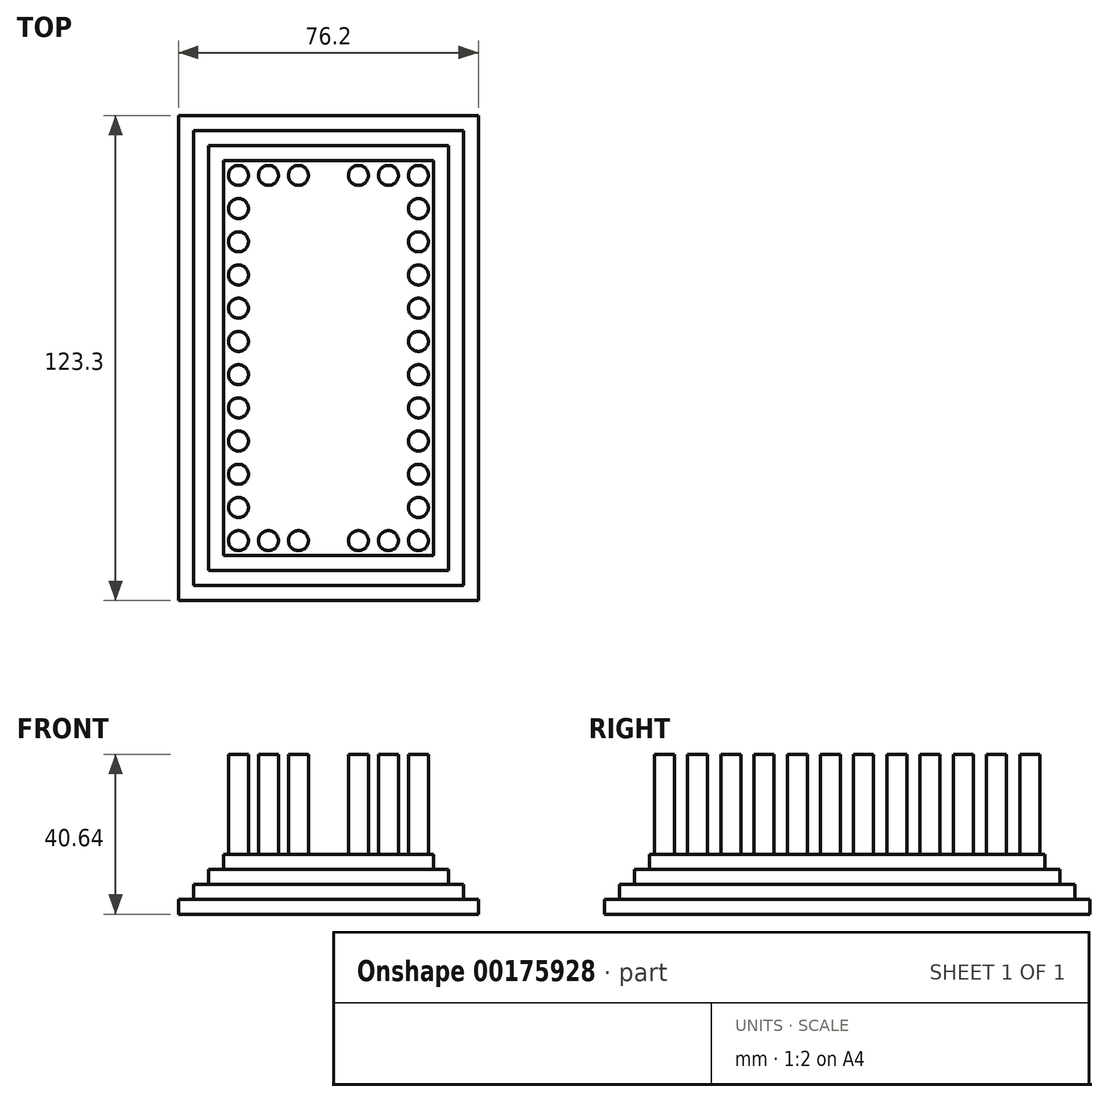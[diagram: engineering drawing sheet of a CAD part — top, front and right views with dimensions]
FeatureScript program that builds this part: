
annotation { "Feature Type Name" : "Feature", "Feature Type Description" : "" }
export const myFeature = defineFeature(function(context is Context, id is Id, definition is map)
    precondition{}
    {
        {
            var Q0;
            Q0=qCreatedBy(makeId("Top.planeOp"),FACE);
            var sketch = newSketch(context, id + "F0", { "sketchPlane" : qUnion([Q0])});
            skLineSegment(sketch, "E0.bottom", {"start": v(38.1, 61.65) * mm, "end": v(-38.1, 61.65) * mm});
            skLineSegment(sketch, "E0.top", {"start": v(38.1, -61.65) * mm, "end": v(-38.1, -61.65) * mm});
            skLineSegment(sketch, "E0.left", {"start": v(38.1, 61.65) * mm, "end": v(38.1, -61.65) * mm});
            skLineSegment(sketch, "E0.right", {"start": v(-38.1, 61.65) * mm, "end": v(-38.1, -61.65) * mm});
            skPoint(sketch, "E0.middle", {"position": v(0, 0) * mm});
            skLineSegment(sketch, "E1.bottom", {"start": v(-34.3, 57.84) * mm, "end": v(34.3, 57.84) * mm});
            skLineSegment(sketch, "E1.top", {"start": v(-34.3, -57.84) * mm, "end": v(34.3, -57.84) * mm});
            skLineSegment(sketch, "E1.left", {"start": v(-34.3, 57.84) * mm, "end": v(-34.3, -57.84) * mm});
            skLineSegment(sketch, "E1.right", {"start": v(34.3, 57.84) * mm, "end": v(34.3, -57.84) * mm});
            skLineSegment(sketch, "E2.bottom", {"start": v(-30.48, 54.03) * mm, "end": v(30.48, 54.03) * mm});
            skLineSegment(sketch, "E2.top", {"start": v(-30.48, -54.03) * mm, "end": v(30.48, -54.03) * mm});
            skLineSegment(sketch, "E2.left", {"start": v(-30.48, 54.03) * mm, "end": v(-30.48, -54.03) * mm});
            skLineSegment(sketch, "E2.right", {"start": v(30.48, 54.03) * mm, "end": v(30.48, -54.03) * mm});
            skLineSegment(sketch, "E3.bottom", {"start": v(26.67, 50.22) * mm, "end": v(-26.67, 50.22) * mm});
            skLineSegment(sketch, "E3.top", {"start": v(26.67, -50.22) * mm, "end": v(-26.67, -50.22) * mm});
            skLineSegment(sketch, "E3.left", {"start": v(26.67, 50.22) * mm, "end": v(26.67, -50.22) * mm});
            skLineSegment(sketch, "E3.right", {"start": v(-26.67, 50.22) * mm, "end": v(-26.67, -50.22) * mm});
            skSolve(sketch);
        }
        {
            var Q0;
            Q0=makeQuery(id+"F0.imprint","IMPRINT",FACE,{"disambiguationData":[TD([[makeQuery(id+"F0.imprint","IMPRINT",EDGE,{"derivedFrom":sQuery(id+"F0.wireOp",EDGE,"E0.bottom")}),1.0]])]});
            extrude(context, id + "F1", {"entities" : qUnion([Q0]), "depth" : 3.8 * mm});
        }
        {
            var Q0;
            Q0=makeQuery(id+"F0.imprint","IMPRINT",FACE,{"disambiguationData":[TD([[makeQuery(id+"F0.imprint","IMPRINT",EDGE,{"derivedFrom":sQuery(id+"F0.wireOp",EDGE,"E1.bottom")}),-1.0]])]});
            extrude(context, id + "F2", {"entities" : qUnion([Q0]), "operationType" : NewBodyOperationType.ADD, "depth" : 7.62 * mm});
        }
        {
            var Q0;
            Q0=makeQuery(id+"F0.imprint","IMPRINT",FACE,{"disambiguationData":[TD([[makeQuery(id+"F0.imprint","IMPRINT",EDGE,{"derivedFrom":sQuery(id+"F0.wireOp",EDGE,"E2.bottom")}),-1.0]])]});
            extrude(context, id + "F3", {"entities" : qUnion([Q0]), "operationType" : NewBodyOperationType.ADD, "depth" : 11.43 * mm});
        }
        {
            var Q0;
            Q0=makeQuery(id+"F0.imprint","IMPRINT",FACE,{"disambiguationData":[TD([[makeQuery(id+"F0.imprint","IMPRINT",EDGE,{"derivedFrom":sQuery(id+"F0.wireOp",EDGE,"E3.bottom")}),1.0]])]});
            extrude(context, id + "F4", {"entities" : qUnion([Q0]), "operationType" : NewBodyOperationType.ADD, "depth" : 15.24 * mm});
        }
        {
            var Q0;
            Q0=makeQuery(id+"F4.opExtrude","CAP_FACE",FACE,{"disambiguationData":[OSD([sQuery(id+"F0.wireOp",EDGE,"E3.bottom"),sQuery(id+"F0.wireOp",EDGE,"E3.top"),sQuery(id+"F0.wireOp",EDGE,"E3.left"),sQuery(id+"F0.wireOp",EDGE,"E3.right")])],"isStart":false});
            var sketch = newSketch(context, id + "F5", { "sketchPlane" : qUnion([Q0])});
            skPoint(sketch, "E4.middle", {"position": v(0, 0) * mm});
            skCircle(sketch, "E5", {"center": v(-22.86, 46.4) * mm, "radius": 2.54 * mm});
            skCircle(sketch, "E6", {"center": v(22.86, 46.4) * mm, "radius": 2.54 * mm});
            skCircle(sketch, "E7", {"center": v(-22.86, -46.4) * mm, "radius": 2.54 * mm});
            skCircle(sketch, "E8", {"center": v(22.86, -46.4) * mm, "radius": 2.54 * mm});
            skPoint(sketch, "E9", {"position": v(0, 46.4) * mm});
            skCircle(sketch, "E10", {"center": v(-15.24, 46.4) * mm, "radius": 2.54 * mm});
            skCircle(sketch, "E11", {"center": v(-7.62, 46.4) * mm, "radius": 2.54 * mm});
            skCircle(sketch, "E12", {"center": v(7.62, 46.4) * mm, "radius": 2.54 * mm});
            skCircle(sketch, "E13", {"center": v(15.24, 46.4) * mm, "radius": 2.54 * mm});
            skCircle(sketch, "E14", {"center": v(-15.24, -46.4) * mm, "radius": 2.54 * mm});
            skCircle(sketch, "E15", {"center": v(-7.62, -46.4) * mm, "radius": 2.54 * mm});
            skCircle(sketch, "E16", {"center": v(7.62, -46.4) * mm, "radius": 2.54 * mm});
            skCircle(sketch, "E17", {"center": v(15.24, -46.4) * mm, "radius": 2.54 * mm});
            skCircle(sketch, "E18", {"center": v(-22.86, -37.97) * mm, "radius": 2.54 * mm});
            skCircle(sketch, "E19", {"center": v(-22.86, -29.53) * mm, "radius": 2.54 * mm});
            skCircle(sketch, "E20", {"center": v(-22.86, -21.1) * mm, "radius": 2.54 * mm});
            skCircle(sketch, "E21", {"center": v(-22.86, -12.66) * mm, "radius": 2.54 * mm});
            skCircle(sketch, "E22", {"center": v(-22.86, -4.22) * mm, "radius": 2.54 * mm});
            skCircle(sketch, "E23", {"center": v(-22.86, 4.22) * mm, "radius": 2.54 * mm});
            skCircle(sketch, "E24", {"center": v(-22.86, 12.66) * mm, "radius": 2.54 * mm});
            skCircle(sketch, "E25", {"center": v(-22.86, 21.1) * mm, "radius": 2.54 * mm});
            skCircle(sketch, "E26", {"center": v(-22.86, 29.53) * mm, "radius": 2.54 * mm});
            skCircle(sketch, "E27", {"center": v(-22.86, 37.96) * mm, "radius": 2.54 * mm});
            skCircle(sketch, "E28", {"center": v(22.86, -37.97) * mm, "radius": 2.54 * mm});
            skCircle(sketch, "E29", {"center": v(22.86, -29.53) * mm, "radius": 2.54 * mm});
            skCircle(sketch, "E30", {"center": v(22.86, -21.1) * mm, "radius": 2.54 * mm});
            skCircle(sketch, "E31", {"center": v(22.86, -12.66) * mm, "radius": 2.54 * mm});
            skCircle(sketch, "E32", {"center": v(22.86, -4.22) * mm, "radius": 2.54 * mm});
            skCircle(sketch, "E33", {"center": v(22.86, 4.22) * mm, "radius": 2.54 * mm});
            skCircle(sketch, "E34", {"center": v(22.86, 12.66) * mm, "radius": 2.54 * mm});
            skCircle(sketch, "E35", {"center": v(22.86, 21.1) * mm, "radius": 2.54 * mm});
            skCircle(sketch, "E36", {"center": v(22.86, 29.53) * mm, "radius": 2.54 * mm});
            skCircle(sketch, "E37", {"center": v(22.86, 37.97) * mm, "radius": 2.54 * mm});
            skSolve(sketch);
        }
        {
            var Q0;
            Q0=makeQuery(id+"F5.imprint","IMPRINT",FACE,{"disambiguationData":[TD([[makeQuery(id+"F5.imprint","IMPRINT",EDGE,{"derivedFrom":sQuery(id+"F5.wireOp",EDGE,"E10")}),1.0]])]});
            var Q1;
            Q1=makeQuery(id+"F5.imprint","IMPRINT",FACE,{"disambiguationData":[TD([[makeQuery(id+"F5.imprint","IMPRINT",EDGE,{"derivedFrom":sQuery(id+"F5.wireOp",EDGE,"E5")}),1.0]])]});
            var Q2;
            Q2=makeQuery(id+"F5.imprint","IMPRINT",FACE,{"disambiguationData":[TD([[makeQuery(id+"F5.imprint","IMPRINT",EDGE,{"derivedFrom":sQuery(id+"F5.wireOp",EDGE,"E11")}),1.0]])]});
            var Q3;
            Q3=makeQuery(id+"F5.imprint","IMPRINT",FACE,{"disambiguationData":[TD([[makeQuery(id+"F5.imprint","IMPRINT",EDGE,{"derivedFrom":sQuery(id+"F5.wireOp",EDGE,"E27")}),1.0]])]});
            var Q4;
            Q4=makeQuery(id+"F5.imprint","IMPRINT",FACE,{"disambiguationData":[TD([[makeQuery(id+"F5.imprint","IMPRINT",EDGE,{"derivedFrom":sQuery(id+"F5.wireOp",EDGE,"E26")}),1.0]])]});
            var Q5;
            Q5=makeQuery(id+"F5.imprint","IMPRINT",FACE,{"disambiguationData":[TD([[makeQuery(id+"F5.imprint","IMPRINT",EDGE,{"derivedFrom":sQuery(id+"F5.wireOp",EDGE,"E25")}),1.0]])]});
            var Q6;
            Q6=makeQuery(id+"F5.imprint","IMPRINT",FACE,{"disambiguationData":[TD([[makeQuery(id+"F5.imprint","IMPRINT",EDGE,{"derivedFrom":sQuery(id+"F5.wireOp",EDGE,"E24")}),1.0]])]});
            var Q7;
            Q7=makeQuery(id+"F5.imprint","IMPRINT",FACE,{"disambiguationData":[TD([[makeQuery(id+"F5.imprint","IMPRINT",EDGE,{"derivedFrom":sQuery(id+"F5.wireOp",EDGE,"E23")}),1.0]])]});
            var Q8;
            Q8=makeQuery(id+"F5.imprint","IMPRINT",FACE,{"disambiguationData":[TD([[makeQuery(id+"F5.imprint","IMPRINT",EDGE,{"derivedFrom":sQuery(id+"F5.wireOp",EDGE,"E22")}),1.0]])]});
            var Q9;
            Q9=makeQuery(id+"F5.imprint","IMPRINT",FACE,{"disambiguationData":[TD([[makeQuery(id+"F5.imprint","IMPRINT",EDGE,{"derivedFrom":sQuery(id+"F5.wireOp",EDGE,"E21")}),1.0]])]});
            var Q10;
            Q10=makeQuery(id+"F5.imprint","IMPRINT",FACE,{"disambiguationData":[TD([[makeQuery(id+"F5.imprint","IMPRINT",EDGE,{"derivedFrom":sQuery(id+"F5.wireOp",EDGE,"E12")}),1.0]])]});
            var Q11;
            Q11=makeQuery(id+"F5.imprint","IMPRINT",FACE,{"disambiguationData":[TD([[makeQuery(id+"F5.imprint","IMPRINT",EDGE,{"derivedFrom":sQuery(id+"F5.wireOp",EDGE,"E13")}),1.0]])]});
            var Q12;
            Q12=makeQuery(id+"F5.imprint","IMPRINT",FACE,{"disambiguationData":[TD([[makeQuery(id+"F5.imprint","IMPRINT",EDGE,{"derivedFrom":sQuery(id+"F5.wireOp",EDGE,"E6")}),1.0]])]});
            var Q13;
            Q13=makeQuery(id+"F5.imprint","IMPRINT",FACE,{"disambiguationData":[TD([[makeQuery(id+"F5.imprint","IMPRINT",EDGE,{"derivedFrom":sQuery(id+"F5.wireOp",EDGE,"E37")}),1.0]])]});
            var Q14;
            Q14=makeQuery(id+"F5.imprint","IMPRINT",FACE,{"disambiguationData":[TD([[makeQuery(id+"F5.imprint","IMPRINT",EDGE,{"derivedFrom":sQuery(id+"F5.wireOp",EDGE,"E36")}),1.0]])]});
            var Q15;
            Q15=makeQuery(id+"F5.imprint","IMPRINT",FACE,{"disambiguationData":[TD([[makeQuery(id+"F5.imprint","IMPRINT",EDGE,{"derivedFrom":sQuery(id+"F5.wireOp",EDGE,"E35")}),1.0]])]});
            var Q16;
            Q16=makeQuery(id+"F5.imprint","IMPRINT",FACE,{"disambiguationData":[TD([[makeQuery(id+"F5.imprint","IMPRINT",EDGE,{"derivedFrom":sQuery(id+"F5.wireOp",EDGE,"E34")}),1.0]])]});
            var Q17;
            Q17=makeQuery(id+"F5.imprint","IMPRINT",FACE,{"disambiguationData":[TD([[makeQuery(id+"F5.imprint","IMPRINT",EDGE,{"derivedFrom":sQuery(id+"F5.wireOp",EDGE,"E33")}),1.0]])]});
            var Q18;
            Q18=makeQuery(id+"F5.imprint","IMPRINT",FACE,{"disambiguationData":[TD([[makeQuery(id+"F5.imprint","IMPRINT",EDGE,{"derivedFrom":sQuery(id+"F5.wireOp",EDGE,"E32")}),1.0]])]});
            var Q19;
            Q19=makeQuery(id+"F5.imprint","IMPRINT",FACE,{"disambiguationData":[TD([[makeQuery(id+"F5.imprint","IMPRINT",EDGE,{"derivedFrom":sQuery(id+"F5.wireOp",EDGE,"E31")}),1.0]])]});
            var Q20;
            Q20=makeQuery(id+"F5.imprint","IMPRINT",FACE,{"disambiguationData":[TD([[makeQuery(id+"F5.imprint","IMPRINT",EDGE,{"derivedFrom":sQuery(id+"F5.wireOp",EDGE,"E20")}),1.0]])]});
            var Q21;
            Q21=makeQuery(id+"F5.imprint","IMPRINT",FACE,{"disambiguationData":[TD([[makeQuery(id+"F5.imprint","IMPRINT",EDGE,{"derivedFrom":sQuery(id+"F5.wireOp",EDGE,"E19")}),1.0]])]});
            var Q22;
            Q22=makeQuery(id+"F5.imprint","IMPRINT",FACE,{"disambiguationData":[TD([[makeQuery(id+"F5.imprint","IMPRINT",EDGE,{"derivedFrom":sQuery(id+"F5.wireOp",EDGE,"E18")}),1.0]])]});
            var Q23;
            Q23=makeQuery(id+"F5.imprint","IMPRINT",FACE,{"disambiguationData":[TD([[makeQuery(id+"F5.imprint","IMPRINT",EDGE,{"derivedFrom":sQuery(id+"F5.wireOp",EDGE,"E7")}),1.0]])]});
            var Q24;
            Q24=makeQuery(id+"F5.imprint","IMPRINT",FACE,{"disambiguationData":[TD([[makeQuery(id+"F5.imprint","IMPRINT",EDGE,{"derivedFrom":sQuery(id+"F5.wireOp",EDGE,"E14")}),1.0]])]});
            var Q25;
            Q25=makeQuery(id+"F5.imprint","IMPRINT",FACE,{"disambiguationData":[TD([[makeQuery(id+"F5.imprint","IMPRINT",EDGE,{"derivedFrom":sQuery(id+"F5.wireOp",EDGE,"E15")}),1.0]])]});
            var Q26;
            Q26=makeQuery(id+"F5.imprint","IMPRINT",FACE,{"disambiguationData":[TD([[makeQuery(id+"F5.imprint","IMPRINT",EDGE,{"derivedFrom":sQuery(id+"F5.wireOp",EDGE,"E16")}),1.0]])]});
            var Q27;
            Q27=makeQuery(id+"F5.imprint","IMPRINT",FACE,{"disambiguationData":[TD([[makeQuery(id+"F5.imprint","IMPRINT",EDGE,{"derivedFrom":sQuery(id+"F5.wireOp",EDGE,"E17")}),1.0]])]});
            var Q28;
            Q28=makeQuery(id+"F5.imprint","IMPRINT",FACE,{"disambiguationData":[TD([[makeQuery(id+"F5.imprint","IMPRINT",EDGE,{"derivedFrom":sQuery(id+"F5.wireOp",EDGE,"E8")}),1.0]])]});
            var Q29;
            Q29=makeQuery(id+"F5.imprint","IMPRINT",FACE,{"disambiguationData":[TD([[makeQuery(id+"F5.imprint","IMPRINT",EDGE,{"derivedFrom":sQuery(id+"F5.wireOp",EDGE,"E28")}),1.0]])]});
            var Q30;
            Q30=makeQuery(id+"F5.imprint","IMPRINT",FACE,{"disambiguationData":[TD([[makeQuery(id+"F5.imprint","IMPRINT",EDGE,{"derivedFrom":sQuery(id+"F5.wireOp",EDGE,"E29")}),1.0]])]});
            var Q31;
            Q31=makeQuery(id+"F5.imprint","IMPRINT",FACE,{"disambiguationData":[TD([[makeQuery(id+"F5.imprint","IMPRINT",EDGE,{"derivedFrom":sQuery(id+"F5.wireOp",EDGE,"E30")}),1.0]])]});
            extrude(context, id + "F6", {"entities" : qUnion([Q0, Q1, Q2, Q3, Q4, Q5, Q6, Q7, Q8, Q9, Q10, Q11, Q12, Q13, Q14, Q15, Q16, Q17, Q18, Q19, Q20, Q21, Q22, Q23, Q24, Q25, Q26, Q27, Q28, Q29, Q30, Q31]), "operationType" : NewBodyOperationType.ADD, "depth" : 25.4 * mm});
        }
    });
